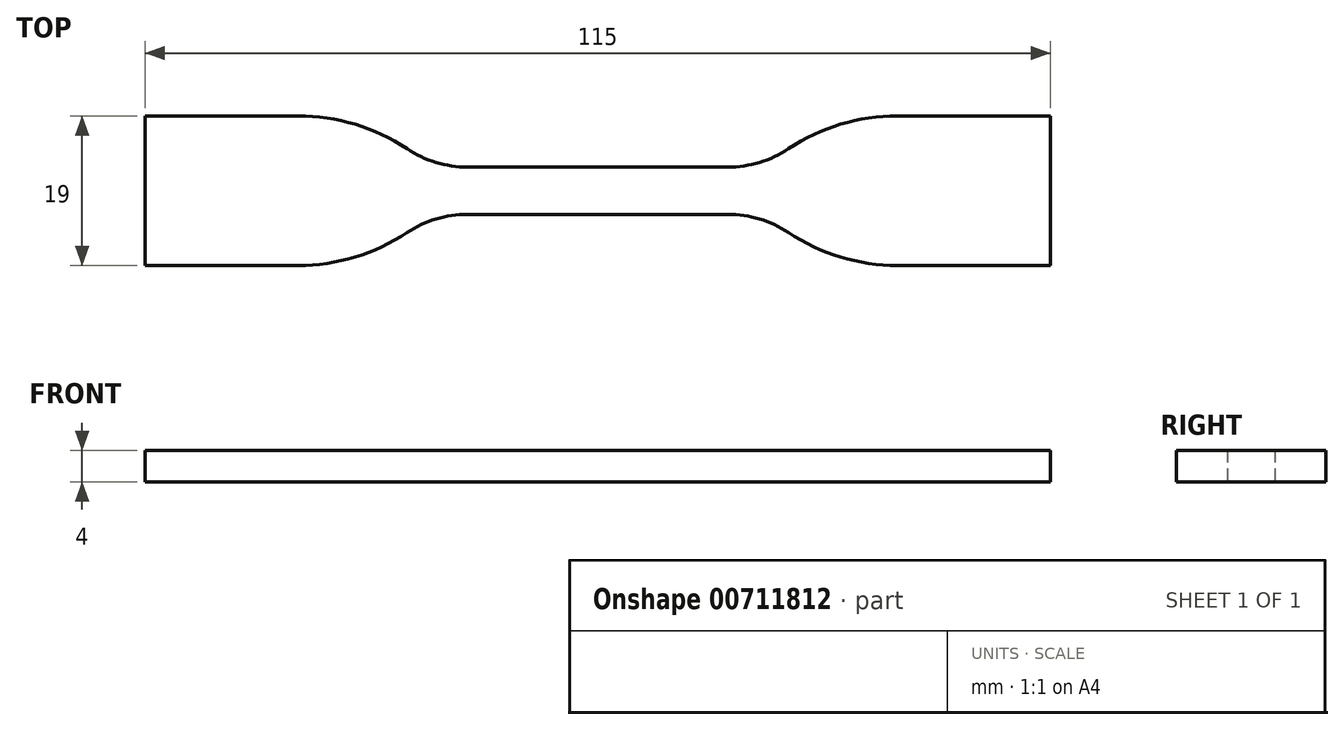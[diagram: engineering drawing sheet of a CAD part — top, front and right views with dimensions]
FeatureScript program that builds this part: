
annotation { "Feature Type Name" : "Feature", "Feature Type Description" : "" }
export const myFeature = defineFeature(function(context is Context, id is Id, definition is map)
    precondition{}
    {
        {
            var Q0;
            Q0=qCreatedBy(makeId("Top.planeOp"),FACE);
            var sketch = newSketch(context, id + "F0", { "sketchPlane" : qUnion([Q0])});
            skLineSegment(sketch, "E0", {"start": v(0, 0) * mm, "end": v(0, 9.5) * mm});
            skLineSegment(sketch, "E1", {"start": v(0, 9.5) * mm, "end": v(19.44, 9.5) * mm});
            skArc(sketch, "E2", {"start": v(33.26, 5.33) * mm, "mid": v(26.66, 8.44) * mm, "end": v(19.44, 9.5) * mm});
            skLineSegment(sketch, "E3", {"start": v(41, 3) * mm, "end": v(74, 3) * mm});
            skPoint(sketch, "E4.visualSharp", {"position": v(36.26, 3) * mm});
            skArc(sketch, "E4.filletArc", {"start": v(33.26, 5.33) * mm, "mid": v(36.96, 3.6) * mm, "end": v(41, 3) * mm});
            skLineSegment(sketch, "E5", {"start": v(115, 0) * mm, "end": v(115, 9.5) * mm});
            skLineSegment(sketch, "E6", {"start": v(115, 9.5) * mm, "end": v(95.56, 9.5) * mm});
            skArc(sketch, "E7", {"start": v(95.56, 9.5) * mm, "mid": v(88.34, 8.44) * mm, "end": v(81.74, 5.33) * mm});
            skPoint(sketch, "E8.visualSharp", {"position": v(78.74, 3) * mm});
            skArc(sketch, "E8.filletArc", {"start": v(74, 3) * mm, "mid": v(78.04, 3.6) * mm, "end": v(81.74, 5.33) * mm});
            skLineSegment(sketch, "E9", {"start": v(0, 0) * mm, "end": v(115, 0) * mm, "construction": true});
            skLineSegment(sketch, "E10.MirrorCS", {"start": v(115, 0) * mm, "end": v(115, -9.5) * mm});
            skLineSegment(sketch, "E11.MirrorCS", {"start": v(115, -9.5) * mm, "end": v(95.56, -9.5) * mm});
            skArc(sketch, "E12.MirrorCS", {"start": v(95.56, -9.5) * mm, "mid": v(88.34, -8.44) * mm, "end": v(81.74, -5.33) * mm});
            skArc(sketch, "E13.MirrorCS", {"start": v(74, -3) * mm, "mid": v(78.04, -3.6) * mm, "end": v(81.74, -5.33) * mm});
            skLineSegment(sketch, "E14.MirrorCS", {"start": v(41, -3) * mm, "end": v(74, -3) * mm});
            skArc(sketch, "E15.MirrorCS", {"start": v(33.26, -5.33) * mm, "mid": v(36.96, -3.6) * mm, "end": v(41, -3) * mm});
            skArc(sketch, "E16.MirrorCS", {"start": v(33.26, -5.33) * mm, "mid": v(26.66, -8.44) * mm, "end": v(19.44, -9.5) * mm});
            skLineSegment(sketch, "E17.MirrorCS", {"start": v(0, -9.5) * mm, "end": v(19.44, -9.5) * mm});
            skLineSegment(sketch, "E18.MirrorCS", {"start": v(0, 0) * mm, "end": v(0, -9.5) * mm});
            skSolve(sketch);
        }
        {
            var Q0;
            Q0 = qSketchRegion(id + "F0", true);
            extrude(context, id + "F1", {"entities" : qUnion([Q0]), "depth" : 4 * mm, "offsetDistance" : 25 * mm});
        }
    });
